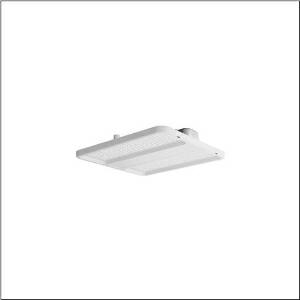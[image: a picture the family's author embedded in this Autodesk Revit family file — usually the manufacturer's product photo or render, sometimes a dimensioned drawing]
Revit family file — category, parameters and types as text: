
# Revit family: highbay_11_midi_51hn11da4eda
name_source: partatom
category: Lighting Fixtures
units: mm (PartAtom-declared; Revit-internal decimal feet)

## family parameters
Cut with Voids When Loaded = No
Host = Face
Light Source = No
Part Type = Normal
Room Calculation Point = No
Round Connector Dimension = Use Diameter
Shared = No

## types (1)
- --- (1 x LED, 1490 lm, 8.2 W, 4000K)
    Apparent Load = 8 VA
    CIE Flux Codes = 85 97 100 100 100
    Color Rendering = 80
    Color Temperature = 4000K
    Default Elevation = 1800 mm
    Description = high bay luminaire Highbay 11 midi; direct symmetric narrow distribution, light control with lens of PMMA; UGR ≤ 19 (X = 4H | Y = 8H | S = 0.25H | reflection values 70/50/20); luminous flux: 10.000lm; light colour: 840, colour temperature: 4000K, MacAdam ≤ 2 SDCM (initial), colour rendering: CRI > 80; luminous efficacy: 209,6lm/W; rated service life: 100.000h (L95/B50) at AT= 25°C; control: DALI 2; housing frame of high-performance plastic PA6, matt traffic white (RAL 9016); cover of PMMA; dimension (LxWxH): 474 x 442 x 72mm; luminaire connection: terminal, 5-pole, max. 2.5mm² (cable entry for one cable, Ø 8.5..16mm); mains connection: 230..240V, AC/DC 0/50..60Hz; connected load: 47,7W; protection rating (complete): IP66; insulation class (complete): insulation class I (protective earthing); protection symbol: D; impact resistance: IK08; halogen-free wiring; for central battery installations according to DIN EN 60598-2-22; corresponds to IFS (International Featured Standards) requirements for safety and quality in the food industry; LABS conformity tested according to VDMA 24364:2018-05; certification: CE, ENEC, VDE, UKCA; permissible operating ambient temperature: -40..+70°C (reducing of maximum allowable ambient temperature of 5°C with ceiling mounting); packaging unit: 1 piece; (delivery without accessories; please order mounting accessories separately)
    Height = 72 mm  [stored 0.23622 ft]
    Lamp = 1 x LED
    Lamp Light Flux = 1490 lm
    Lamp Power = 8.2 W
    Lamp count = 1
    Length = 474 mm
    Luminous efficacy = 182 lm/W
    Manufacturer = Siteco
    ModVariant = No
    Model = 51HN11DA4EDA
    Mounting Place = Ceiling
    Mounting Type = Pendant
    Number of Poles = 1
    OnlyDefault = Yes
    Power Factor = 1
    Product Name = Highbay 11 midi
    Product group = high bay luminaire
    ProductGroupID = 901
    Protection Class = Protection class I
    Protection Degree = IP 66
    RLX_Detail_Level = 1
    RLX_Emergency_Light_Flux = 0 lm
    RLX_Emergency_Type = 0
    RLX_Emergency_Type_DB = No
    RlxData = <blob elided: 16717 chars, md5=430ceec2>
    Socket = socket
    Standby Power = 0 W
    System Light Flux = 1490 lm
    System Power = 8 W
    Type Comments = : DC mode (central or group accumulator) initial emergency light level
    Type Image = l_1363240.jpg
    URL = http://relux.com
    VarID = @adj_003729
    Voltage = 0 V
    Weight = 0.00 kg
    Width = 442 mm

note: [stored X ft] marks values corroborated as IEEE doubles in the binary element streams (Revit-internal decimal feet)

## geometry (parser evidence)
native form markers: Blend x4, Sweep x9
no freeform markers — native parametric forms only
